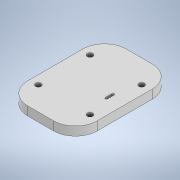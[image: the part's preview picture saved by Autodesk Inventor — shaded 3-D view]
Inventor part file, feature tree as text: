
AUTODESK INVENTOR PART (.ipt)
format: ipt  version: 2020 (Build 240168000, 168)  size: 163,840 bytes
history: native  units: mm
features: extrude x2, sketch x2
ambient origin geometry x8: Origin, YZ Plane, XZ Plane, XY Plane, X Axis, Y Axis, Z Axis, Center Point
bodies: Body1 (feature_tree)
feature tree (4):
  extrude  "Extrusion6"  Depth=39.6mm
  extrude  "Extrusion7"  Depth=4.0mm
  sketch  "Sketch1"  dims[d10=39.6mm d11=39.6mm]
  sketch  "Sketch7"  dims[d62=5.0mm d63=5.0mm d64=5.0mm d65=5.0mm d67=39.6mm d68=39.6mm d72=8.0mm d73=0.0mm d75=4.0mm d76=0.0mm]
